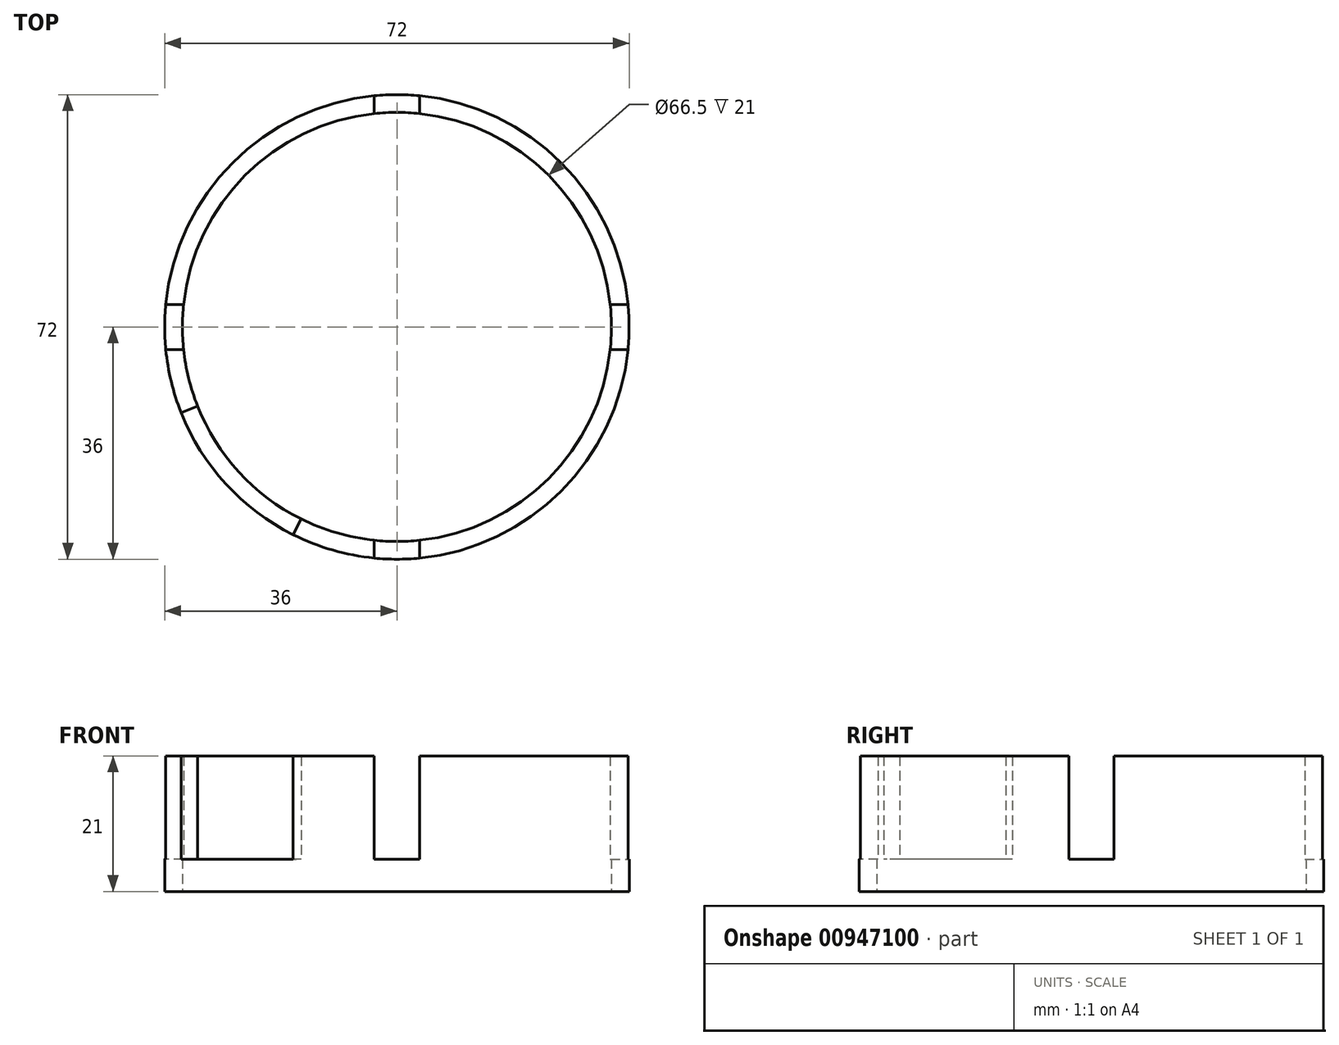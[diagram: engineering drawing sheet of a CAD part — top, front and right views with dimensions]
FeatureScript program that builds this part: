
annotation { "Feature Type Name" : "Feature", "Feature Type Description" : "" }
export const myFeature = defineFeature(function(context is Context, id is Id, definition is map)
    precondition{}
    {
        {
            var Q0;
            Q0=qCreatedBy(makeId("Top.planeOp"),FACE);
            var sketch = newSketch(context, id + "F0", { "sketchPlane" : qUnion([Q0])});
            skCircle(sketch, "E0", {"center": v(0, 0) * mm, "radius": 33.25 * mm});
            skCircle(sketch, "E1", {"center": v(0, 0) * mm, "radius": 36 * mm});
            skSolve(sketch);
        }
        {
            var Q0;
            Q0 = qSketchRegion(id + "F0", true);
            extrude(context, id + "F1", {"entities" : qUnion([Q0]), "depth" : 21 * mm, "offsetDistance" : 25 * mm});
        }
        {
            var Q0;
            Q0=makeQuery(id+"F1.opExtrude","CAP_FACE",FACE,{"disambiguationData":[OSD([sQuery(id+"F0.wireOp",EDGE,"E0"),sQuery(id+"F0.wireOp",EDGE,"E1")])],"isStart":false});
            var sketch = newSketch(context, id + "F2", { "sketchPlane" : qUnion([Q0])});
            skLineSegment(sketch, "E2.bottom", {"start": v(3.5, 27.75) * mm, "end": v(-3.5, 27.75) * mm});
            skLineSegment(sketch, "E2.top", {"start": v(3.5, 38.75) * mm, "end": v(-3.5, 38.75) * mm});
            skLineSegment(sketch, "E2.left", {"start": v(3.5, 27.75) * mm, "end": v(3.5, 38.75) * mm});
            skLineSegment(sketch, "E2.right", {"start": v(-3.5, 27.75) * mm, "end": v(-3.5, 38.75) * mm});
            skPoint(sketch, "E2.middle", {"position": v(0, 33.25) * mm});
            skLineSegment(sketch, "E3.1.0", {"start": v(-38.75, 3.5) * mm, "end": v(-38.75, -3.5) * mm});
            skLineSegment(sketch, "E3.1.1", {"start": v(-27.75, 3.5) * mm, "end": v(-38.75, 3.5) * mm});
            skLineSegment(sketch, "E3.1.2", {"start": v(-27.75, 3.5) * mm, "end": v(-27.75, -3.5) * mm});
            skPoint(sketch, "E3.1.3", {"position": v(-33.25, 0) * mm});
            skLineSegment(sketch, "E3.1.4", {"start": v(-27.75, -3.5) * mm, "end": v(-38.75, -3.5) * mm});
            skLineSegment(sketch, "E3.2.0", {"start": v(-3.5, -38.75) * mm, "end": v(3.5, -38.75) * mm});
            skLineSegment(sketch, "E3.2.1", {"start": v(-3.5, -27.75) * mm, "end": v(-3.5, -38.75) * mm});
            skLineSegment(sketch, "E3.2.2", {"start": v(-3.5, -27.75) * mm, "end": v(3.5, -27.75) * mm});
            skPoint(sketch, "E3.2.3", {"position": v(0, -33.25) * mm});
            skLineSegment(sketch, "E3.2.4", {"start": v(3.5, -27.75) * mm, "end": v(3.5, -38.75) * mm});
            skLineSegment(sketch, "E3.3.0", {"start": v(38.75, -3.5) * mm, "end": v(38.75, 3.5) * mm});
            skLineSegment(sketch, "E3.3.1", {"start": v(27.75, -3.5) * mm, "end": v(38.75, -3.5) * mm});
            skLineSegment(sketch, "E3.3.2", {"start": v(27.75, -3.5) * mm, "end": v(27.75, 3.5) * mm});
            skPoint(sketch, "E3.3.3", {"position": v(33.25, 0) * mm});
            skLineSegment(sketch, "E3.3.4", {"start": v(27.75, 3.5) * mm, "end": v(38.75, 3.5) * mm});
            skPoint(sketch, "E3.center", {"position": v(0, 0) * mm});
            skLineSegment(sketch, "E4", {"start": v(0, 0) * mm, "end": v(-52.63, -20.86) * mm});
            skLineSegment(sketch, "E5", {"start": v(0, 0) * mm, "end": v(-24.27, -48.56) * mm});
            skLineSegment(sketch, "E6", {"start": v(-52.63, -20.86) * mm, "end": v(-24.27, -48.56) * mm});
            skSolve(sketch);
        }
        {
            var Q0;
            Q0 = qSketchRegion(id + "F2", true);
            extrude(context, id + "F3", {"entities" : qUnion([Q0]), "operationType" : NewBodyOperationType.REMOVE, "oppositeDirection" : true, "depth" : 16 * mm, "offsetDistance" : 25 * mm});
        }
    });
